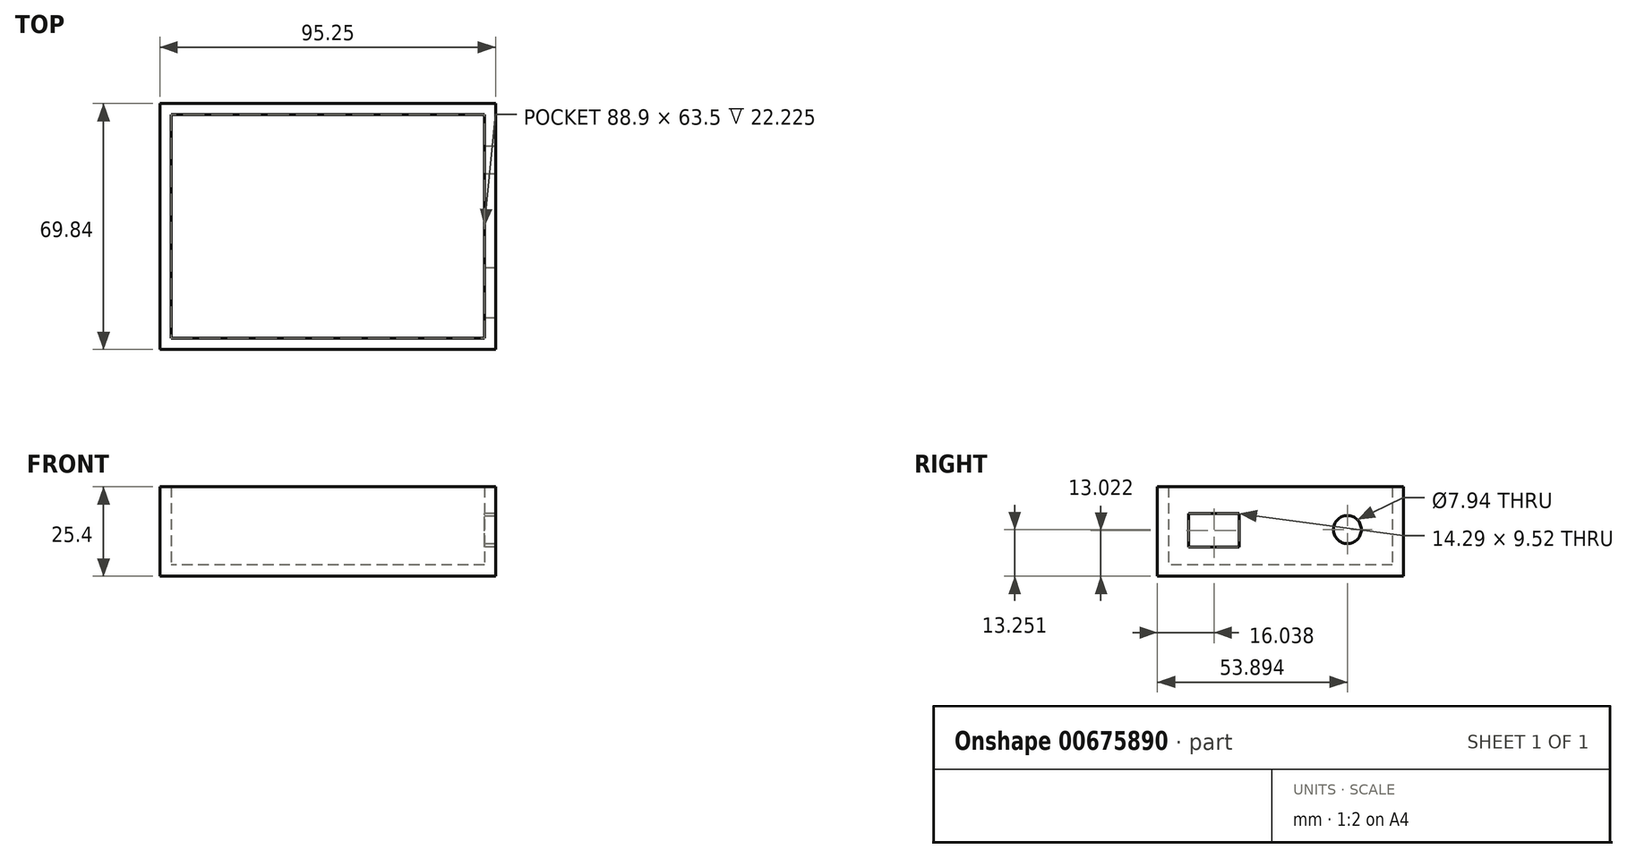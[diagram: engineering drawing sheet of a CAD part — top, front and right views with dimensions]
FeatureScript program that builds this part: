
annotation { "Feature Type Name" : "Feature", "Feature Type Description" : "" }
export const myFeature = defineFeature(function(context is Context, id is Id, definition is map)
    precondition{}
    {
        {
            var Q0;
            Q0=qCreatedBy(makeId("Top.planeOp"),FACE);
            var sketch = newSketch(context, id + "F0", { "sketchPlane" : qUnion([Q0])});
            skLineSegment(sketch, "E0.bottom", {"start": v(47.62, 34.93) * mm, "end": v(-47.63, 34.93) * mm});
            skLineSegment(sketch, "E0.top", {"start": v(47.63, -34.92) * mm, "end": v(-47.62, -34.93) * mm});
            skLineSegment(sketch, "E0.left", {"start": v(47.62, 34.93) * mm, "end": v(47.63, -34.93) * mm});
            skLineSegment(sketch, "E0.right", {"start": v(-47.63, 34.93) * mm, "end": v(-47.62, -34.93) * mm});
            skPoint(sketch, "E0.middle", {"position": v(0, 0) * mm});
            skLineSegment(sketch, "E1.bottom", {"start": v(44.45, 31.75) * mm, "end": v(-44.45, 31.75) * mm});
            skLineSegment(sketch, "E1.top", {"start": v(44.45, -31.75) * mm, "end": v(-44.45, -31.75) * mm});
            skLineSegment(sketch, "E1.left", {"start": v(44.45, 31.75) * mm, "end": v(44.45, -31.75) * mm});
            skLineSegment(sketch, "E1.right", {"start": v(-44.45, 31.75) * mm, "end": v(-44.45, -31.75) * mm});
            skSolve(sketch);
        }
        {
            var Q0;
            Q0=makeQuery(id+"F0.imprint","IMPRINT",FACE,{"disambiguationData":[TD([[makeQuery(id+"F0.imprint","IMPRINT",EDGE,{"derivedFrom":sQuery(id+"F0.wireOp",EDGE,"E0.bottom")}),1.0]])]});
            extrude(context, id + "F1", {"entities" : qUnion([Q0]), "depth" : 25.4 * mm, "offsetDistance" : 25.4 * mm});
        }
        {
            var Q0;
            Q0=makeQuery(id+"F1.opExtrude","SWEPT_FACE",FACE,{"disambiguationData":[OSD([sQuery(id+"F0.wireOp",EDGE,"E0.left")])]});
            var sketch = newSketch(context, id + "F2", { "sketchPlane" : qUnion([Q0])});
            skLineSegment(sketch, "E2.bottom", {"start": v(-26.03, 17.78) * mm, "end": v(-11.74, 17.78) * mm});
            skLineSegment(sketch, "E2.top", {"start": v(-26.03, 8.26) * mm, "end": v(-11.74, 8.26) * mm});
            skLineSegment(sketch, "E2.left", {"start": v(-26.03, 17.78) * mm, "end": v(-26.03, 8.26) * mm});
            skLineSegment(sketch, "E2.right", {"start": v(-11.74, 17.78) * mm, "end": v(-11.74, 8.26) * mm});
            skSolve(sketch);
        }
        {
            var Q0;
            Q0=makeQuery(id+"F0.imprint","IMPRINT",FACE,{"disambiguationData":[TD([[makeQuery(id+"F0.imprint","IMPRINT",EDGE,{"derivedFrom":sQuery(id+"F0.wireOp",EDGE,"E1.bottom")}),1.0]])]});
            extrude(context, id + "F3", {"entities" : qUnion([Q0]), "operationType" : NewBodyOperationType.ADD, "depth" : 3.17 * mm, "offsetDistance" : 25.4 * mm});
        }
        {
            var Q0;
            Q0=makeQuery(id+"F2.imprint","IMPRINT",FACE,{"disambiguationData":[TD([[makeQuery(id+"F2.imprint","IMPRINT",EDGE,{"derivedFrom":sQuery(id+"F2.wireOp",EDGE,"E2.bottom")}),1.0]])]});
            var sketch = newSketch(context, id + "F4", { "sketchPlane" : qUnion([Q0])});
            skPoint(sketch, "E3", {"position": v(18.97, 13.25) * mm});
            skSolve(sketch);
        }
        {
            var Q0;
            Q0=sQuery(id+"F4.wireOp",VERTEX,"E3");
            var Q1;
            Q1=makeQuery(id+"F1.opExtrude","SWEPT_BODY",BODY,{"disambiguationData":[OSD([sQuery(id+"F0.wireOp",EDGE,"E0.bottom"),sQuery(id+"F0.wireOp",EDGE,"E0.top"),sQuery(id+"F0.wireOp",EDGE,"E0.left"),sQuery(id+"F0.wireOp",EDGE,"E0.right"),sQuery(id+"F0.wireOp",EDGE,"E1.bottom"),sQuery(id+"F0.wireOp",EDGE,"E1.top"),sQuery(id+"F0.wireOp",EDGE,"E1.left"),sQuery(id+"F0.wireOp",EDGE,"E1.right")])]});
            hole(context, id + "F5", {"style" : HoleStyle.SIMPLE, "endStyle" : HoleEndStyle.BLIND, "holeDiameter" : 7.94 * mm, "majorDiameter" : 6.35 * mm, "holeDepth" : 12.7 * mm, "isTappedThrough" : true, "tappedDepth" : 12.7 * mm, "tapClearance" : 3, "locations" : qUnion([Q0]), "scope" : qUnion([Q1])});
        }
        {
            var Q0;
            Q0=makeQuery(id+"F2.imprint","IMPRINT",FACE,{"disambiguationData":[TD([[makeQuery(id+"F2.imprint","IMPRINT",EDGE,{"derivedFrom":sQuery(id+"F2.wireOp",EDGE,"E2.bottom")}),-1.0]])]});
            extrude(context, id + "F6", {"entities" : qUnion([Q0]), "operationType" : NewBodyOperationType.REMOVE, "endBound" : BoundingType.SYMMETRIC, "depth" : 25.4 * mm, "offsetDistance" : 25.4 * mm});
        }
    });
